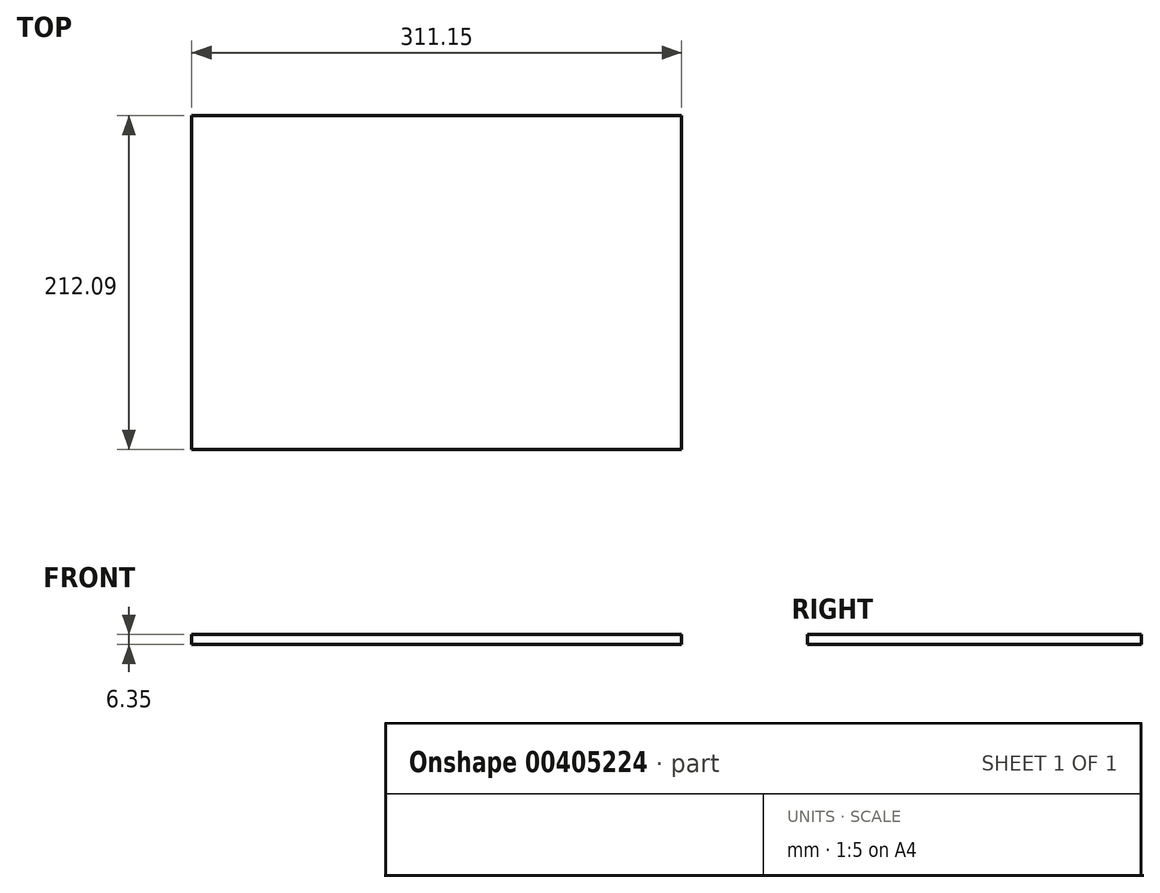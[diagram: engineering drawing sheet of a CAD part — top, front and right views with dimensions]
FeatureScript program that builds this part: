
annotation { "Feature Type Name" : "Feature", "Feature Type Description" : "" }
export const myFeature = defineFeature(function(context is Context, id is Id, definition is map)
    precondition{}
    {
        {
            var Q0;
            Q0=qCreatedBy(makeId("Right.planeOp"),FACE);
            var sketch = newSketch(context, id + "F0", { "sketchPlane" : qUnion([Q0])});
            skLineSegment(sketch, "E0.bottom", {"start": v(-84.6, 9.94) * mm, "end": v(127.5, 9.94) * mm});
            skLineSegment(sketch, "E0.top", {"start": v(-84.6, 3.59) * mm, "end": v(127.5, 3.59) * mm});
            skLineSegment(sketch, "E0.left", {"start": v(-84.6, 9.94) * mm, "end": v(-84.6, 3.59) * mm});
            skLineSegment(sketch, "E0.right", {"start": v(127.5, 9.94) * mm, "end": v(127.5, 3.59) * mm});
            skLineSegment(sketch, "E1.bottom", {"start": v(127.5, 9.94) * mm, "end": v(121.15, 9.94) * mm});
            skLineSegment(sketch, "E1.top", {"start": v(127.5, 17.56) * mm, "end": v(121.15, 17.56) * mm});
            skLineSegment(sketch, "E1.left", {"start": v(127.5, 9.94) * mm, "end": v(127.5, 17.56) * mm});
            skLineSegment(sketch, "E1.right", {"start": v(121.15, 9.94) * mm, "end": v(121.15, 17.56) * mm});
            skLineSegment(sketch, "E2.top", {"start": v(-84.6, -85.31) * mm, "end": v(127.5, -85.31) * mm});
            skLineSegment(sketch, "E2.left", {"start": v(-84.6, 3.59) * mm, "end": v(-84.6, -85.31) * mm});
            skLineSegment(sketch, "E2.right", {"start": v(127.5, 3.59) * mm, "end": v(127.5, -85.31) * mm});
            skLineSegment(sketch, "E3.bottom", {"start": v(-84.6, 9.94) * mm, "end": v(-78.24, 9.94) * mm});
            skLineSegment(sketch, "E3.top", {"start": v(-84.6, 70.9) * mm, "end": v(-78.24, 70.9) * mm});
            skLineSegment(sketch, "E3.left", {"start": v(-84.6, 9.94) * mm, "end": v(-84.6, 70.9) * mm});
            skLineSegment(sketch, "E3.right", {"start": v(-78.24, 9.94) * mm, "end": v(-78.24, 70.9) * mm});
            skSolve(sketch);
        }
        {
            var Q0;
            Q0=makeQuery(id+"F0.imprint","IMPRINT",FACE,{"disambiguationData":[TD([[makeQuery(id+"F0.imprint","IMPRINT",EDGE,{"derivedFrom":sQuery(id+"F0.wireOp",EDGE,"E0.top")}),-1.0]])]});
            var Q1;
            Q1=makeQuery(id+"F0.imprint","IMPRINT",FACE,{"disambiguationData":[TD([[makeQuery(id+"F0.imprint","IMPRINT",EDGE,{"derivedFrom":sQuery(id+"F0.wireOp",EDGE,"E0.bottom")}),-1.0]])]});
            var Q2;
            Q2=makeQuery(id+"F0.imprint","IMPRINT",FACE,{"disambiguationData":[TD([[makeQuery(id+"F0.imprint","IMPRINT",EDGE,{"derivedFrom":sQuery(id+"F0.wireOp",EDGE,"E1.bottom")}),-1.0]])]});
            var Q3;
            Q3=makeQuery(id+"F0.imprint","IMPRINT",FACE,{"disambiguationData":[TD([[makeQuery(id+"F0.imprint","IMPRINT",EDGE,{"derivedFrom":sQuery(id+"F0.wireOp",EDGE,"E3.bottom")}),1.0]])]});
            extrude(context, id + "F1", {"entities" : qUnion([Q0, Q1, Q2, Q3]), "depth" : 311.15 * mm});
        }
        {
            var Q0;
            Q0=qCreatedBy(makeId("Front.planeOp"),FACE);
            var sketch = newSketch(context, id + "F2", { "sketchPlane" : qUnion([Q0])});
            skLineSegment(sketch, "E4.bottom", {"start": v(0, 9.94) * mm, "end": v(6.35, 9.94) * mm, "construction": true});
            skLineSegment(sketch, "E4.top", {"start": v(0, 3.59) * mm, "end": v(6.35, 3.59) * mm, "construction": true});
            skLineSegment(sketch, "E4.left", {"start": v(0, 9.94) * mm, "end": v(0, 3.59) * mm, "construction": true});
            skLineSegment(sketch, "E4.right", {"start": v(6.35, 9.94) * mm, "end": v(6.35, 3.59) * mm, "construction": true});
            skPoint(sketch, "E5", {"position": v(0, 9.94) * mm});
            skLineSegment(sketch, "E6.bottom", {"start": v(6.35, 3.59) * mm, "end": v(304.8, 3.59) * mm});
            skLineSegment(sketch, "E6.top", {"start": v(6.35, -85.31) * mm, "end": v(304.8, -85.31) * mm});
            skLineSegment(sketch, "E6.left", {"start": v(6.35, 3.59) * mm, "end": v(6.35, -85.31) * mm});
            skLineSegment(sketch, "E6.right", {"start": v(304.8, 3.59) * mm, "end": v(304.8, -85.31) * mm});
            skSolve(sketch);
        }
        {
            var Q0;
            Q0=makeQuery(id+"F2.imprint","IMPRINT",FACE,{"disambiguationData":[TD([[makeQuery(id+"F2.imprint","IMPRINT",EDGE,{"derivedFrom":sQuery(id+"F2.wireOp",EDGE,"E6.bottom")}),-1.0]])]});
            extrude(context, id + "F3", {"entities" : qUnion([Q0]), "operationType" : NewBodyOperationType.REMOVE, "endBound" : BoundingType.SYMMETRIC, "depth" : 303.28 * mm});
        }
    });
